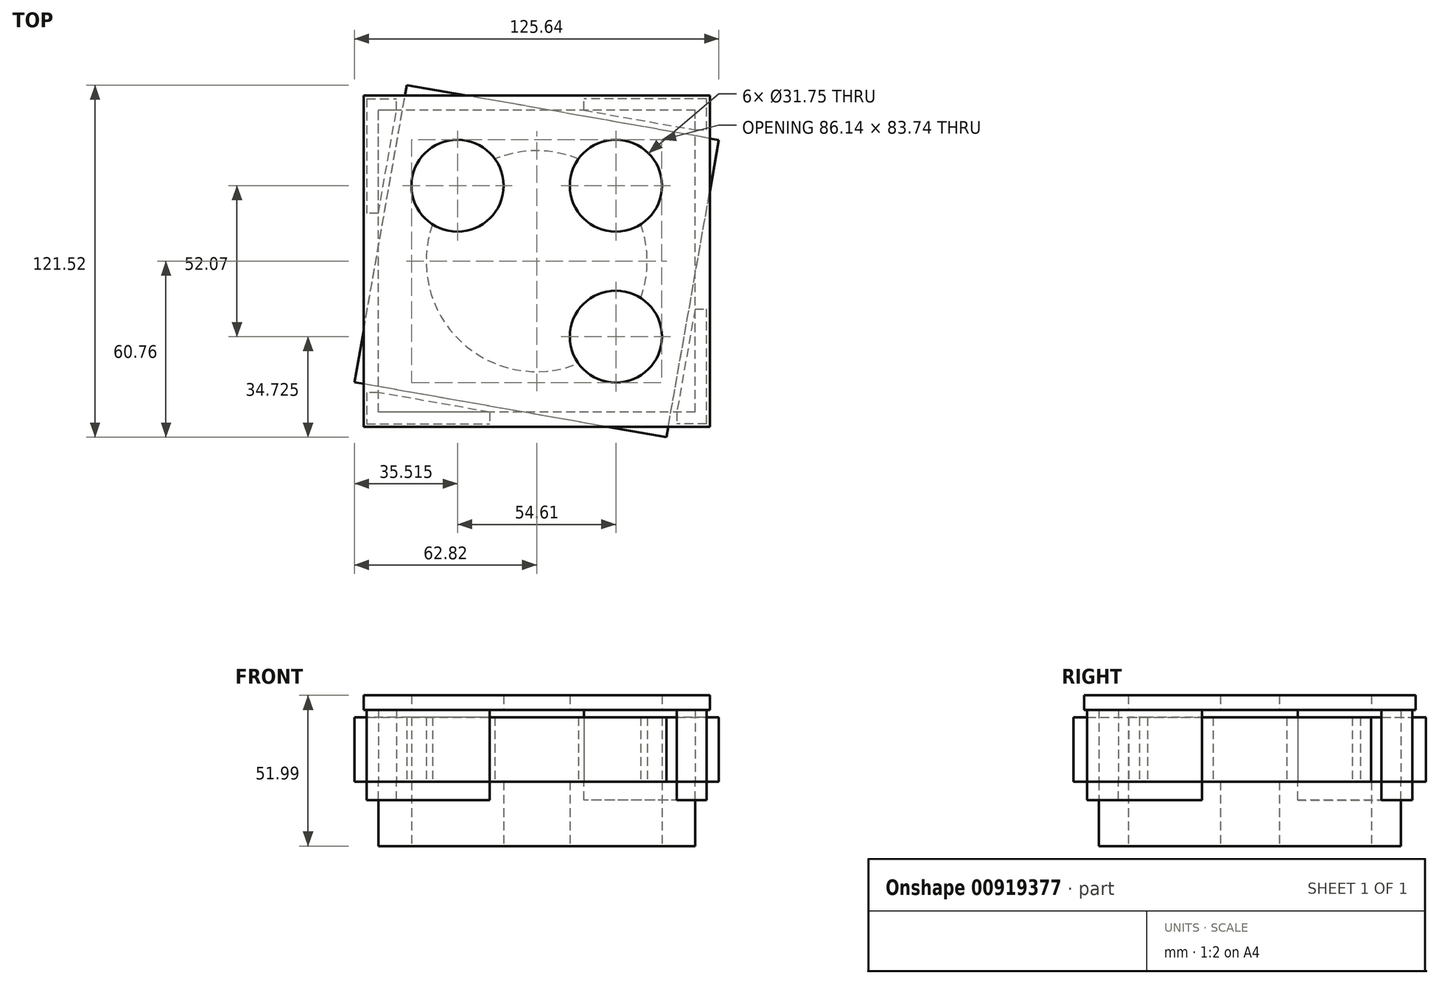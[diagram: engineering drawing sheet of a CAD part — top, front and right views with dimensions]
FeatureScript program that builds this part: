
annotation { "Feature Type Name" : "Feature", "Feature Type Description" : "" }
export const myFeature = defineFeature(function(context is Context, id is Id, definition is map)
    precondition{}
    {
        {
            var Q0;
            Q0=qCreatedBy(makeId("Top.planeOp"),FACE);
            var sketch = newSketch(context, id + "F0", { "sketchPlane" : qUnion([Q0])});
            skLineSegment(sketch, "E0.bottom", {"start": v(54.61, -52.07) * mm, "end": v(-54.6, -52.07) * mm});
            skLineSegment(sketch, "E0.top", {"start": v(54.61, 52.07) * mm, "end": v(-54.6, 52.07) * mm});
            skLineSegment(sketch, "E0.left", {"start": v(54.61, -52.07) * mm, "end": v(54.61, 52.07) * mm});
            skLineSegment(sketch, "E0.right", {"start": v(-54.6, -52.07) * mm, "end": v(-54.6, 52.07) * mm});
            skPoint(sketch, "E0.middle", {"position": v(0, 0) * mm});
            skSolve(sketch);
        }
        {
            var Q0;
            Q0 = qSketchRegion(id + "F0", true);
            extrude(context, id + "F1", {"entities" : qUnion([Q0]), "depth" : 22.22 * mm, "offsetDistance" : 25.4 * mm});
        }
        {
            var Q0;
            Q0=makeQuery(id+"F1.opExtrude","CAP_FACE",FACE,{"disambiguationData":[OSD([sQuery(id+"F0.wireOp",EDGE,"E0.bottom"),sQuery(id+"F0.wireOp",EDGE,"E0.top"),sQuery(id+"F0.wireOp",EDGE,"E0.left"),sQuery(id+"F0.wireOp",EDGE,"E0.right"),sQuery(id+"F0.wireOp",EDGE,"pyYYmUB0-zl6w-7IVd-MrnJ-UJeOwzH38l0g")])],"isStart":false});
            var sketch = newSketch(context, id + "F2", { "sketchPlane" : qUnion([Q0])});
            skLineSegment(sketch, "E1.bottom", {"start": v(44.74, -60.76) * mm, "end": v(-62.82, -41.8) * mm});
            skLineSegment(sketch, "E1.top", {"start": v(62.82, 41.8) * mm, "end": v(-44.74, 60.76) * mm});
            skLineSegment(sketch, "E1.left", {"start": v(44.74, -60.76) * mm, "end": v(62.82, 41.8) * mm});
            skLineSegment(sketch, "E1.right", {"start": v(-62.82, -41.8) * mm, "end": v(-44.74, 60.76) * mm});
            skPoint(sketch, "E1.middle", {"position": v(0, 0) * mm});
            skCircle(sketch, "E2", {"center": v(0, 0) * mm, "radius": 38.1 * mm});
            skSolve(sketch);
        }
        {
            var Q0;
            {var subQ0=sQuery(id+"F2.wireOp",EDGE,"E1.left");var subQ1=sQuery(id+"F2.wireOp",EDGE,"E1.bottom");var subQ2=makeQuery(id+"F2.imprint","INTERSECT",VERTEX,{"derivedFrom":[subQ1,subQ0]});Q0=makeQuery(id+"F2.imprint","IMPRINT",FACE,{"disambiguationData":[TD([[makeQuery(id+"F2.imprint","IMPRINT",EDGE,{"disambiguationData":[TD([[subQ2,-1.0]])],"derivedFrom":subQ1}),-1.0]])]});}
            var Q1;
            Q1=makeQuery(id+"F2.imprint","IMPRINT",FACE,{"disambiguationData":[TD([[makeQuery(id+"F2.imprint","IMPRINT",EDGE,{"derivedFrom":sQuery(id+"F2.wireOp",EDGE,"E2")}),-1.0]])]});
            var Q2;
            {var subQ0=sQuery(id+"F2.wireOp",EDGE,"E1.left");var subQ1=sQuery(id+"F2.wireOp",EDGE,"E1.top");var subQ2=makeQuery(id+"F2.imprint","INTERSECT",VERTEX,{"derivedFrom":[subQ1,subQ0]});Q2=makeQuery(id+"F2.imprint","IMPRINT",FACE,{"disambiguationData":[TD([[makeQuery(id+"F2.imprint","IMPRINT",EDGE,{"disambiguationData":[TD([[subQ2,-1.0]])],"derivedFrom":subQ1}),1.0]])]});}
            var Q3;
            {var subQ0=sQuery(id+"F2.wireOp",EDGE,"E1.right");var subQ1=sQuery(id+"F2.wireOp",EDGE,"E1.top");var subQ2=makeQuery(id+"F2.imprint","INTERSECT",VERTEX,{"derivedFrom":[subQ1,subQ0]});Q3=makeQuery(id+"F2.imprint","IMPRINT",FACE,{"disambiguationData":[TD([[makeQuery(id+"F2.imprint","IMPRINT",EDGE,{"disambiguationData":[TD([[subQ2,1.0]])],"derivedFrom":subQ1}),1.0]])]});}
            var Q4;
            {var subQ0=sQuery(id+"F2.wireOp",EDGE,"E1.right");var subQ1=sQuery(id+"F2.wireOp",EDGE,"E1.bottom");var subQ2=makeQuery(id+"F2.imprint","INTERSECT",VERTEX,{"derivedFrom":[subQ1,subQ0]});Q4=makeQuery(id+"F2.imprint","IMPRINT",FACE,{"disambiguationData":[TD([[makeQuery(id+"F2.imprint","IMPRINT",EDGE,{"disambiguationData":[TD([[subQ2,1.0]])],"derivedFrom":subQ1}),-1.0]])]});}
            extrude(context, id + "F3", {"entities" : qUnion([Q0, Q1, Q2, Q3, Q4]), "depth" : 22.22 * mm, "offsetDistance" : 25.4 * mm});
        }
        {
            var Q0;
            Q0=makeQuery(id+"F1.opExtrude","CAP_FACE",FACE,{"disambiguationData":[OSD([sQuery(id+"F0.wireOp",EDGE,"E0.bottom"),sQuery(id+"F0.wireOp",EDGE,"E0.top"),sQuery(id+"F0.wireOp",EDGE,"E0.left"),sQuery(id+"F0.wireOp",EDGE,"E0.right"),sQuery(id+"F0.wireOp",EDGE,"pyYYmUB0-zl6w-7IVd-MrnJ-UJeOwzH38l0g")])],"isStart":false});
            var sketch = newSketch(context, id + "F4", { "sketchPlane" : qUnion([Q0])});
            skLineSegment(sketch, "E3", {"start": v(-54.6, 52.07) * mm, "end": v(-54.6, 16.48) * mm});
            skLineSegment(sketch, "E4", {"start": v(-54.61, 16.48) * mm, "end": v(-48.33, 52.07) * mm});
            skLineSegment(sketch, "E5", {"start": v(-48.33, 52.07) * mm, "end": v(-54.6, 52.07) * mm});
            skPoint(sketch, "E6.center", {"position": v(0, 0) * mm});
            skLineSegment(sketch, "E7", {"start": v(54.61, 52.07) * mm, "end": v(16.26, 52.07) * mm});
            skLineSegment(sketch, "E8", {"start": v(16.26, 52.07) * mm, "end": v(54.61, 45.3) * mm});
            skLineSegment(sketch, "E9.bottom", {"start": v(-54.6, 52.07) * mm, "end": v(-48.33, 52.07) * mm});
            skLineSegment(sketch, "E9.top", {"start": v(-54.6, 56.07) * mm, "end": v(-48.33, 56.07) * mm});
            skLineSegment(sketch, "E9.left", {"start": v(-54.6, 52.07) * mm, "end": v(-54.6, 56.07) * mm});
            skLineSegment(sketch, "E9.right", {"start": v(-48.33, 52.07) * mm, "end": v(-48.33, 56.07) * mm});
            skLineSegment(sketch, "E10.bottom", {"start": v(-54.6, 56.07) * mm, "end": v(-58.6, 56.07) * mm});
            skLineSegment(sketch, "E10.top", {"start": v(-54.6, 16.48) * mm, "end": v(-58.6, 16.48) * mm});
            skLineSegment(sketch, "E10.left", {"start": v(-54.6, 56.07) * mm, "end": v(-54.6, 16.48) * mm});
            skLineSegment(sketch, "E10.right", {"start": v(-58.6, 56.07) * mm, "end": v(-58.6, 16.48) * mm});
            skLineSegment(sketch, "E11.bottom", {"start": v(54.61, 45.3) * mm, "end": v(58.61, 45.3) * mm});
            skLineSegment(sketch, "E11.top", {"start": v(54.61, 52.07) * mm, "end": v(58.61, 52.07) * mm});
            skLineSegment(sketch, "E11.left", {"start": v(54.61, 45.3) * mm, "end": v(54.61, 52.07) * mm});
            skLineSegment(sketch, "E11.right", {"start": v(58.61, 45.3) * mm, "end": v(58.61, 52.07) * mm});
            skLineSegment(sketch, "E12.bottom", {"start": v(58.61, 52.07) * mm, "end": v(16.26, 52.07) * mm});
            skLineSegment(sketch, "E12.top", {"start": v(58.61, 56.07) * mm, "end": v(16.26, 56.07) * mm});
            skLineSegment(sketch, "E12.left", {"start": v(58.61, 52.07) * mm, "end": v(58.61, 56.07) * mm});
            skLineSegment(sketch, "E12.right", {"start": v(16.26, 52.07) * mm, "end": v(16.26, 56.07) * mm});
            skLineSegment(sketch, "E13.1.0", {"start": v(54.61, -56.07) * mm, "end": v(58.61, -56.07) * mm});
            skLineSegment(sketch, "E13.1.1", {"start": v(58.61, -56.07) * mm, "end": v(58.61, -16.48) * mm});
            skLineSegment(sketch, "E13.1.2", {"start": v(54.61, -16.48) * mm, "end": v(58.61, -16.48) * mm});
            skLineSegment(sketch, "E13.1.3", {"start": v(54.61, -56.07) * mm, "end": v(54.61, -16.48) * mm});
            skLineSegment(sketch, "E13.1.4", {"start": v(54.61, -16.48) * mm, "end": v(48.33, -52.07) * mm});
            skLineSegment(sketch, "E13.1.5", {"start": v(54.61, -52.07) * mm, "end": v(48.33, -52.07) * mm});
            skLineSegment(sketch, "E13.1.6", {"start": v(54.61, -56.07) * mm, "end": v(48.33, -56.07) * mm});
            skLineSegment(sketch, "E13.1.7", {"start": v(48.33, -52.07) * mm, "end": v(48.33, -56.07) * mm});
            skLineSegment(sketch, "E13.1.8", {"start": v(-58.6, -56.07) * mm, "end": v(-16.26, -56.07) * mm});
            skLineSegment(sketch, "E13.1.9", {"start": v(-16.26, -52.07) * mm, "end": v(-16.26, -56.07) * mm});
            skLineSegment(sketch, "E13.1.10", {"start": v(-16.26, -52.07) * mm, "end": v(-54.6, -45.3) * mm});
            skLineSegment(sketch, "E13.1.11", {"start": v(-54.6, -45.3) * mm, "end": v(-58.6, -45.3) * mm});
            skLineSegment(sketch, "E13.1.12", {"start": v(-54.6, -45.3) * mm, "end": v(-54.6, -52.07) * mm});
            skLineSegment(sketch, "E13.1.13", {"start": v(-58.6, -52.07) * mm, "end": v(-16.26, -52.07) * mm});
            skLineSegment(sketch, "E13.1.14", {"start": v(-58.6, -45.3) * mm, "end": v(-58.6, -52.07) * mm});
            skLineSegment(sketch, "E13.1.15", {"start": v(-58.6, -52.07) * mm, "end": v(-58.6, -56.07) * mm});
            skSolve(sketch);
        }
        {
            var Q0;
            Q0=makeQuery(id+"F4.imprint","IMPRINT",FACE,{"disambiguationData":[TD([[makeQuery(id+"F4.imprint","IMPRINT",EDGE,{"derivedFrom":sQuery(id+"F4.wireOp",EDGE,"E5")}),-1.0]])]});
            var Q1;
            Q1=makeQuery(id+"F4.imprint","IMPRINT",FACE,{"disambiguationData":[TD([[makeQuery(id+"F4.imprint","IMPRINT",EDGE,{"derivedFrom":sQuery(id+"F4.wireOp",EDGE,"E3")}),1.0]])]});
            var Q2;
            Q2=makeQuery(id+"F4.imprint","IMPRINT",FACE,{"disambiguationData":[TD([[makeQuery(id+"F4.imprint","IMPRINT",EDGE,{"derivedFrom":sQuery(id+"F4.wireOp",EDGE,"E13.1.11")}),1.0]])]});
            var Q3;
            Q3=makeQuery(id+"F4.imprint","IMPRINT",FACE,{"disambiguationData":[TD([[makeQuery(id+"F4.imprint","IMPRINT",EDGE,{"derivedFrom":sQuery(id+"F4.wireOp",EDGE,"E13.1.8")}),1.0]])]});
            var Q4;
            {var subQ0=sQuery(id+"F4.wireOp",EDGE,"E13.1.5");Q4=makeQuery(id+"F4.imprint","IMPRINT",FACE,{"disambiguationData":[TD([[makeQuery(id+"F4.imprint","IMPRINT",EDGE,{"derivedFrom":subQ0}),1.0]])]});}
            var Q5;
            {var subQ3=sQuery(id+"F4.wireOp",EDGE,"E13.1.0");Q5=makeQuery(id+"F4.imprint","IMPRINT",FACE,{"disambiguationData":[TD([[makeQuery(id+"F4.imprint","IMPRINT",EDGE,{"derivedFrom":subQ3}),1.0]])]});}
            var Q6;
            Q6=makeQuery(id+"F4.imprint","IMPRINT",FACE,{"disambiguationData":[TD([[makeQuery(id+"F4.imprint","IMPRINT",EDGE,{"derivedFrom":sQuery(id+"F4.wireOp",EDGE,"E7")}),-1.0]])]});
            var Q7;
            Q7=makeQuery(id+"F4.imprint","IMPRINT",FACE,{"disambiguationData":[TD([[makeQuery(id+"F4.imprint","IMPRINT",EDGE,{"derivedFrom":sQuery(id+"F4.wireOp",EDGE,"E11.bottom")}),1.0]])]});
            extrude(context, id + "F5", {"entities" : qUnion([Q0, Q1, Q2, Q3, Q4, Q5, Q6, Q7]), "oppositeDirection" : true, "depth" : 6.35 * mm, "offsetDistance" : 25.4 * mm});
        }
        {
            var Q0;
            {var subQ2=sQuery(id+"F4.wireOp",EDGE,"E13.1.4");Q0=makeQuery(id+"F4.imprint","IMPRINT",FACE,{"disambiguationData":[TD([[makeQuery(id+"F4.imprint","IMPRINT",EDGE,{"derivedFrom":subQ2}),1.0]])]});}
            var Q1;
            Q1=makeQuery(id+"F4.imprint","IMPRINT",FACE,{"disambiguationData":[TD([[makeQuery(id+"F4.imprint","IMPRINT",EDGE,{"derivedFrom":sQuery(id+"F4.wireOp",EDGE,"E7")}),1.0]])]});
            var Q2;
            Q2=makeQuery(id+"F4.imprint","IMPRINT",FACE,{"disambiguationData":[TD([[makeQuery(id+"F4.imprint","IMPRINT",EDGE,{"derivedFrom":sQuery(id+"F4.wireOp",EDGE,"E3")}),-1.0]])]});
            var Q3;
            {var subQ0=sQuery(id+"F4.wireOp",EDGE,"E13.1.10");Q3=makeQuery(id+"F4.imprint","IMPRINT",FACE,{"disambiguationData":[TD([[makeQuery(id+"F4.imprint","IMPRINT",EDGE,{"derivedFrom":subQ0}),1.0]])]});}
            var Q4;
            Q4=makeQuery(id+"F5.opExtrude","CAP_FACE",FACE,{"disambiguationData":[OSD([sQuery(id+"F4.wireOp",EDGE,"E7"),sQuery(id+"F4.wireOp",EDGE,"E11.bottom"),sQuery(id+"F4.wireOp",EDGE,"E11.left"),sQuery(id+"F4.wireOp",EDGE,"E11.right"),sQuery(id+"F4.wireOp",EDGE,"E12.top"),sQuery(id+"F4.wireOp",EDGE,"E12.left"),sQuery(id+"F4.wireOp",EDGE,"E12.right")])],"isStart":true});
            var Q5;
            Q5=makeQuery(id+"F5.opExtrude","CAP_FACE",FACE,{"disambiguationData":[OSD([sQuery(id+"F4.wireOp",EDGE,"E13.1.0"),sQuery(id+"F4.wireOp",EDGE,"E13.1.1"),sQuery(id+"F4.wireOp",EDGE,"E13.1.2"),sQuery(id+"F4.wireOp",EDGE,"E13.1.3"),sQuery(id+"F4.wireOp",EDGE,"E13.1.5"),sQuery(id+"F4.wireOp",EDGE,"E13.1.6"),sQuery(id+"F4.wireOp",EDGE,"E13.1.7")])],"isStart":true});
            var Q6;
            Q6=makeQuery(id+"F5.opExtrude","CAP_FACE",FACE,{"disambiguationData":[OSD([sQuery(id+"F4.wireOp",EDGE,"E13.1.8"),sQuery(id+"F4.wireOp",EDGE,"E13.1.9"),sQuery(id+"F4.wireOp",EDGE,"E13.1.11"),sQuery(id+"F4.wireOp",EDGE,"E13.1.12"),sQuery(id+"F4.wireOp",EDGE,"E13.1.13"),sQuery(id+"F4.wireOp",EDGE,"E13.1.14"),sQuery(id+"F4.wireOp",EDGE,"E13.1.15")])],"isStart":true});
            var Q7;
            Q7=makeQuery(id+"F5.opExtrude","CAP_FACE",FACE,{"disambiguationData":[OSD([sQuery(id+"F4.wireOp",EDGE,"E3"),sQuery(id+"F4.wireOp",EDGE,"E5"),sQuery(id+"F4.wireOp",EDGE,"E9.top"),sQuery(id+"F4.wireOp",EDGE,"E9.right"),sQuery(id+"F4.wireOp",EDGE,"E10.bottom"),sQuery(id+"F4.wireOp",EDGE,"E10.top"),sQuery(id+"F4.wireOp",EDGE,"E10.right")])],"isStart":true});
            extrude(context, id + "F6", {"entities" : qUnion([Q0, Q1, Q2, Q3, Q4, Q5, Q6, Q7]), "depth" : 25.4 * mm, "offsetDistance" : 25.4 * mm});
        }
        {
            var Q0;
            Q0=qCreatedBy(makeId("Top.planeOp"),FACE);
            cPlane(context, id + "F7", {"entities" : qUnion([Q0]), "cplaneType" : CPlaneType.OFFSET, "offset" : 47 * mm, "width" : 152.4 * mm, "height" : 152.4 * mm});
        }
        {
            var Q0;
            Q0=qCreatedBy(id+"F7.planeOp",FACE);
            var sketch = newSketch(context, id + "F8", { "sketchPlane" : qUnion([Q0])});
            skLineSegment(sketch, "E14.bottom", {"start": v(59.69, -57.15) * mm, "end": v(-59.7, -57.15) * mm});
            skLineSegment(sketch, "E14.top", {"start": v(59.7, 57.15) * mm, "end": v(-59.69, 57.15) * mm});
            skLineSegment(sketch, "E14.left", {"start": v(59.69, -57.15) * mm, "end": v(59.7, 57.15) * mm});
            skLineSegment(sketch, "E14.right", {"start": v(-59.7, -57.15) * mm, "end": v(-59.69, 57.15) * mm});
            skPoint(sketch, "E14.middle", {"position": v(0, 0) * mm});
            skSolve(sketch);
        }
        {
            var Q0;
            Q0 = qSketchRegion(id + "F8", true);
            extrude(context, id + "F9", {"entities" : qUnion([Q0]), "operationType" : NewBodyOperationType.ADD, "depth" : 5 * mm, "offsetDistance" : 25.4 * mm});
        }
        {
            var Q0;
            Q0=makeQuery(id+"F1.opExtrude","CAP_FACE",FACE,{"disambiguationData":[OSD([sQuery(id+"F0.wireOp",EDGE,"E0.bottom"),sQuery(id+"F0.wireOp",EDGE,"E0.top"),sQuery(id+"F0.wireOp",EDGE,"E0.left"),sQuery(id+"F0.wireOp",EDGE,"E0.right")])],"isStart":true});
            var sketch = newSketch(context, id + "F10", { "sketchPlane" : qUnion([Q0])});
            skLineSegment(sketch, "E15", {"start": v(0, 0) * mm, "end": v(-54.61, 52.07) * mm});
            skLineSegment(sketch, "E16", {"start": v(-54.6, 52.07) * mm, "end": v(54.61, -52.07) * mm});
            skLineSegment(sketch, "E17", {"start": v(-54.61, -52.07) * mm, "end": v(54.61, 52.07) * mm});
            skCircle(sketch, "E18", {"center": v(-27.3, -26.04) * mm, "radius": 15.88 * mm});
            skCircle(sketch, "E19", {"center": v(27.3, -26.04) * mm, "radius": 15.88 * mm});
            skCircle(sketch, "E20", {"center": v(-27.3, 26.03) * mm, "radius": 15.88 * mm});
            skCircle(sketch, "E21", {"center": v(27.3, 26.03) * mm, "radius": 15.88 * mm});
            skSolve(sketch);
        }
        {
            var Q0;
            {var subQ0=sQuery(id+"F10.wireOp",EDGE,"E20");var subQ1=sQuery(id+"F10.wireOp",EDGE,"E16");var subQ2=makeQuery(id+"F10.imprint","INTERSECT",VERTEX,{"disambiguationData":[OD(0.0)],"derivedFrom":[subQ1,subQ0]});Q0=makeQuery(id+"F10.imprint","IMPRINT",FACE,{"disambiguationData":[TD([[makeQuery(id+"F10.imprint","IMPRINT",EDGE,{"disambiguationData":[TD([[subQ2,-1.0]])],"derivedFrom":subQ1}),-1.0]])]});}
            var Q1;
            {var subQ0=sQuery(id+"F10.wireOp",EDGE,"E20");var subQ1=sQuery(id+"F10.wireOp",EDGE,"E16");var subQ2=makeQuery(id+"F10.imprint","INTERSECT",VERTEX,{"disambiguationData":[OD(0.0)],"derivedFrom":[subQ1,subQ0]});Q1=makeQuery(id+"F10.imprint","IMPRINT",FACE,{"disambiguationData":[TD([[makeQuery(id+"F10.imprint","IMPRINT",EDGE,{"disambiguationData":[TD([[subQ2,-1.0]])],"derivedFrom":subQ1}),1.0]])]});}
            var Q2;
            {var subQ0=sQuery(id+"F10.wireOp",EDGE,"E18");var subQ1=sQuery(id+"F10.wireOp",EDGE,"E17");var subQ2=makeQuery(id+"F10.imprint","INTERSECT",VERTEX,{"disambiguationData":[OD(0.0)],"derivedFrom":[subQ1,subQ0]});Q2=makeQuery(id+"F10.imprint","IMPRINT",FACE,{"disambiguationData":[TD([[makeQuery(id+"F10.imprint","IMPRINT",EDGE,{"disambiguationData":[TD([[subQ2,-1.0]])],"derivedFrom":subQ1}),1.0]])]});}
            var Q3;
            {var subQ0=sQuery(id+"F10.wireOp",EDGE,"E18");var subQ1=sQuery(id+"F10.wireOp",EDGE,"E17");var subQ2=makeQuery(id+"F10.imprint","INTERSECT",VERTEX,{"disambiguationData":[OD(0.0)],"derivedFrom":[subQ1,subQ0]});Q3=makeQuery(id+"F10.imprint","IMPRINT",FACE,{"disambiguationData":[TD([[makeQuery(id+"F10.imprint","IMPRINT",EDGE,{"disambiguationData":[TD([[subQ2,-1.0]])],"derivedFrom":subQ1}),-1.0]])]});}
            var Q4;
            {var subQ0=sQuery(id+"F10.wireOp",EDGE,"E19");var subQ1=sQuery(id+"F10.wireOp",EDGE,"E16");var subQ2=makeQuery(id+"F10.imprint","INTERSECT",VERTEX,{"disambiguationData":[OD(0.0)],"derivedFrom":[subQ1,subQ0]});Q4=makeQuery(id+"F10.imprint","IMPRINT",FACE,{"disambiguationData":[TD([[makeQuery(id+"F10.imprint","IMPRINT",EDGE,{"disambiguationData":[TD([[subQ2,-1.0]])],"derivedFrom":subQ1}),-1.0]])]});}
            var Q5;
            {var subQ0=sQuery(id+"F10.wireOp",EDGE,"E19");var subQ1=sQuery(id+"F10.wireOp",EDGE,"E16");var subQ2=makeQuery(id+"F10.imprint","INTERSECT",VERTEX,{"disambiguationData":[OD(0.0)],"derivedFrom":[subQ1,subQ0]});Q5=makeQuery(id+"F10.imprint","IMPRINT",FACE,{"disambiguationData":[TD([[makeQuery(id+"F10.imprint","IMPRINT",EDGE,{"disambiguationData":[TD([[subQ2,-1.0]])],"derivedFrom":subQ1}),1.0]])]});}
            var Q6;
            {var subQ0=sQuery(id+"F10.wireOp",EDGE,"E21");var subQ1=sQuery(id+"F10.wireOp",EDGE,"E17");var subQ2=makeQuery(id+"F10.imprint","INTERSECT",VERTEX,{"disambiguationData":[OD(0.0)],"derivedFrom":[subQ1,subQ0]});Q6=makeQuery(id+"F10.imprint","IMPRINT",FACE,{"disambiguationData":[TD([[makeQuery(id+"F10.imprint","IMPRINT",EDGE,{"disambiguationData":[TD([[subQ2,-1.0]])],"derivedFrom":subQ1}),-1.0]])]});}
            var Q7;
            {var subQ0=sQuery(id+"F10.wireOp",EDGE,"E21");var subQ1=sQuery(id+"F10.wireOp",EDGE,"E17");var subQ2=makeQuery(id+"F10.imprint","INTERSECT",VERTEX,{"disambiguationData":[OD(0.0)],"derivedFrom":[subQ1,subQ0]});Q7=makeQuery(id+"F10.imprint","IMPRINT",FACE,{"disambiguationData":[TD([[makeQuery(id+"F10.imprint","IMPRINT",EDGE,{"disambiguationData":[TD([[subQ2,-1.0]])],"derivedFrom":subQ1}),1.0]])]});}
            extrude(context, id + "F11", {"entities" : qUnion([Q0, Q1, Q2, Q3, Q4, Q5, Q6, Q7]), "operationType" : NewBodyOperationType.REMOVE, "oppositeDirection" : true, "depth" : 89.4 * mm, "offsetDistance" : 25.4 * mm});
        }
    });
